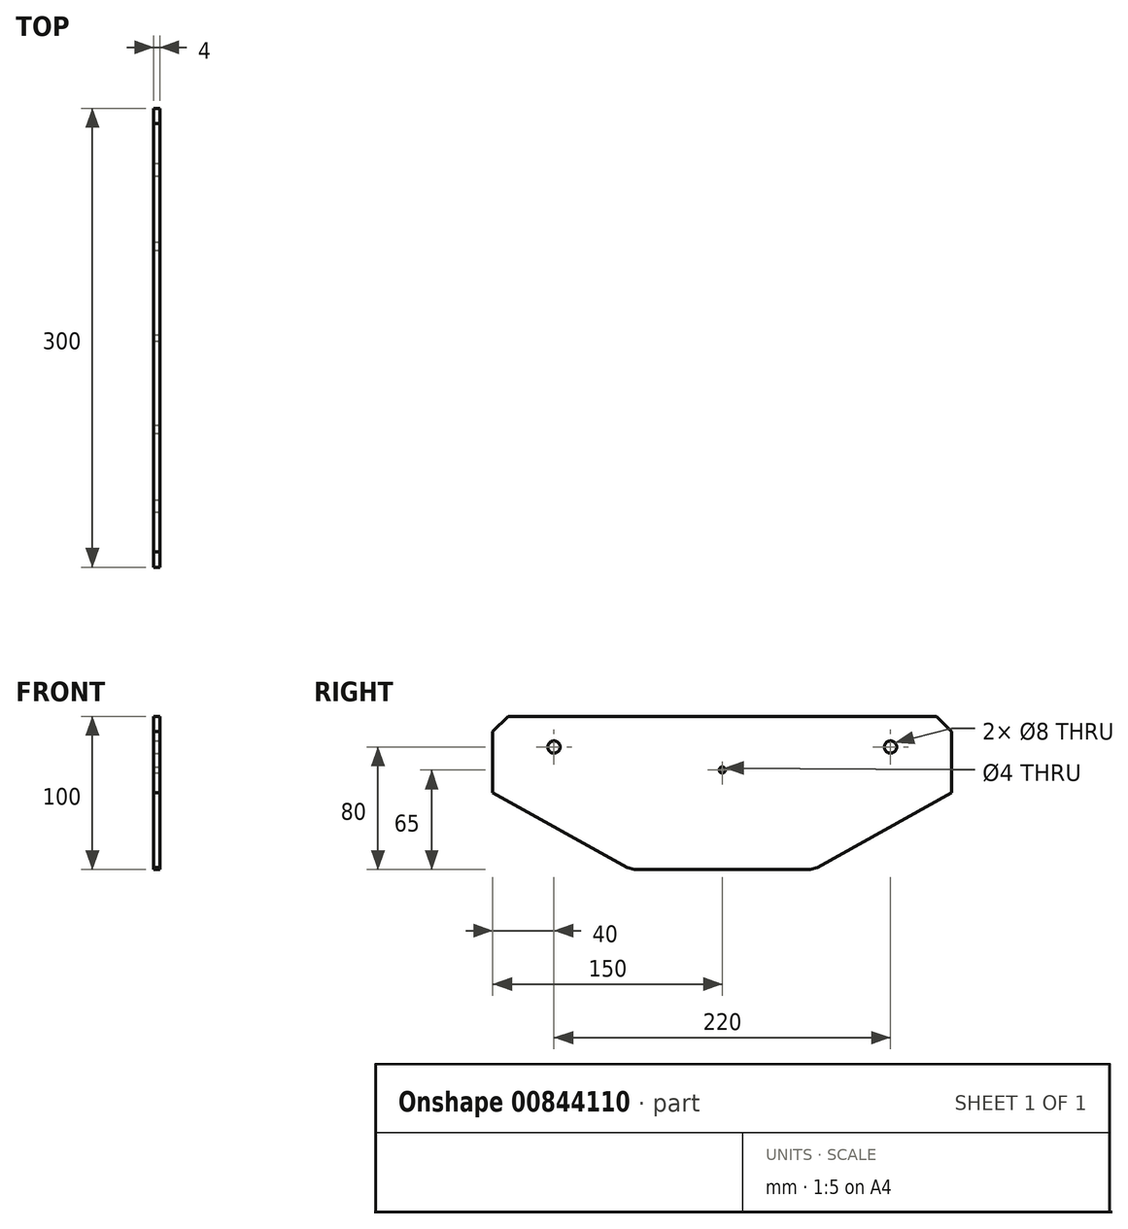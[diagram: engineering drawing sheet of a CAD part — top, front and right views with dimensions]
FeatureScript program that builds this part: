
annotation { "Feature Type Name" : "Feature", "Feature Type Description" : "" }
export const myFeature = defineFeature(function(context is Context, id is Id, definition is map)
    precondition{}
    {
        {
            var Q0;
            Q0=qCreatedBy(makeId("Right.planeOp"),FACE);
            var sketch = newSketch(context, id + "F0", { "sketchPlane" : qUnion([Q0])});
            skLineSegment(sketch, "E0", {"start": v(-150, 100) * mm, "end": v(150, 100) * mm});
            skLineSegment(sketch, "E1", {"start": v(150, 100) * mm, "end": v(150, 50) * mm});
            skLineSegment(sketch, "E2", {"start": v(150, 50) * mm, "end": v(60, 0) * mm});
            skLineSegment(sketch, "E3", {"start": v(60, 0) * mm, "end": v(-60, 0) * mm});
            skLineSegment(sketch, "E4", {"start": v(-60, 0) * mm, "end": v(-150, 50) * mm});
            skLineSegment(sketch, "E5", {"start": v(-150, 50) * mm, "end": v(-150, 100) * mm});
            skSolve(sketch);
        }
        {
            var Q0;
            Q0=makeQuery(id+"F0.imprint","IMPRINT",FACE,{"disambiguationData":[TD([[makeQuery(id+"F0.imprint","IMPRINT",EDGE,{"derivedFrom":sQuery(id+"F0.wireOp",EDGE,"E0")}),-1.0]])]});
            extrude(context, id + "F1", {"entities" : qUnion([Q0]), "endBound" : BoundingType.SYMMETRIC, "depth" : 4 * mm, "offsetDistance" : 25.4 * mm});
        }
        {
            var Q0;
            Q0=makeQuery(id+"F1.opExtrude","CAP_FACE",FACE,{"disambiguationData":[OSD([sQuery(id+"F0.wireOp",EDGE,"E0"),sQuery(id+"F0.wireOp",EDGE,"E1"),sQuery(id+"F0.wireOp",EDGE,"E2"),sQuery(id+"F0.wireOp",EDGE,"E3"),sQuery(id+"F0.wireOp",EDGE,"E4"),sQuery(id+"F0.wireOp",EDGE,"E5")])],"isStart":false});
            var sketch = newSketch(context, id + "F2", { "sketchPlane" : qUnion([Q0])});
            skPoint(sketch, "E6", {"position": v(-110, 80) * mm});
            skPoint(sketch, "E7", {"position": v(110, 80) * mm});
            skPoint(sketch, "E8", {"position": v(-60, -20) * mm});
            skPoint(sketch, "E9", {"position": v(60, -20) * mm});
            skPoint(sketch, "E10", {"position": v(0, -20) * mm});
            skPoint(sketch, "E11", {"position": v(0, 65) * mm});
            skSolve(sketch);
        }
        {
            var Q0;
            Q0=sQuery(id+"F2.wireOp",VERTEX,"E6");
            var Q1;
            Q1=sQuery(id+"F2.wireOp",VERTEX,"E7");
            var Q2;
            Q2=makeQuery(id+"F1.opExtrude","SWEPT_BODY",BODY,{"disambiguationData":[OSD([sQuery(id+"F0.wireOp",EDGE,"E0"),sQuery(id+"F0.wireOp",EDGE,"E1"),sQuery(id+"F0.wireOp",EDGE,"E2"),sQuery(id+"F0.wireOp",EDGE,"E3"),sQuery(id+"F0.wireOp",EDGE,"E4"),sQuery(id+"F0.wireOp",EDGE,"E5")])]});
            hole(context, id + "F3", {"style" : HoleStyle.SIMPLE, "endStyle" : HoleEndStyle.THROUGH, "holeDiameter" : 8 * mm, "majorDiameter" : 6.35 * mm, "isTappedThrough" : true, "tappedDepth" : 12.7 * mm, "tapClearance" : 3, "locations" : qUnion([Q0, Q1]), "scope" : qUnion([Q2])});
        }
        {
            var Q0;
            Q0=sQuery(id+"F2.wireOp",VERTEX,"E8");
            var Q1;
            Q1=sQuery(id+"F2.wireOp",VERTEX,"E10");
            var Q2;
            Q2=sQuery(id+"F2.wireOp",VERTEX,"E9");
            var Q3;
            Q3=makeQuery(id+"F1.opExtrude","SWEPT_BODY",BODY,{"disambiguationData":[OSD([sQuery(id+"F0.wireOp",EDGE,"E0"),sQuery(id+"F0.wireOp",EDGE,"E1"),sQuery(id+"F0.wireOp",EDGE,"E2"),sQuery(id+"F0.wireOp",EDGE,"E3"),sQuery(id+"F0.wireOp",EDGE,"E4"),sQuery(id+"F0.wireOp",EDGE,"E5")])]});
            hole(context, id + "F4", {"style" : HoleStyle.SIMPLE, "endStyle" : HoleEndStyle.THROUGH, "holeDiameter" : 4 * mm, "majorDiameter" : 6.35 * mm, "isTappedThrough" : true, "tappedDepth" : 12.7 * mm, "tapClearance" : 3, "locations" : qUnion([Q0, Q1, Q2]), "scope" : qUnion([Q3])});
        }
        {
            var Q0;
            Q0=makeQuery(id+"F1.opExtrude","SWEPT_EDGE",EDGE,{"disambiguationData":[OSD([sQuery(id+"F0.wireOp",EDGE,"E0"),sQuery(id+"F0.wireOp",EDGE,"E1")])]});
            var Q1;
            Q1=makeQuery(id+"F1.opExtrude","SWEPT_EDGE",EDGE,{"disambiguationData":[OSD([sQuery(id+"F0.wireOp",EDGE,"E0"),sQuery(id+"F0.wireOp",EDGE,"E5")])]});
            var Q2;
            Q2=makeQuery(id+"F1.opExtrude","SWEPT_EDGE",EDGE,{"disambiguationData":[OSD([sQuery(id+"F0.wireOp",EDGE,"E3"),sQuery(id+"F0.wireOp",EDGE,"E4")])]});
            var Q3;
            Q3=makeQuery(id+"F1.opExtrude","SWEPT_EDGE",EDGE,{"disambiguationData":[OSD([sQuery(id+"F0.wireOp",EDGE,"E2"),sQuery(id+"F0.wireOp",EDGE,"E3")])]});
            chamfer(context, id + "F5", {"entities" : qUnion([Q0, Q1, Q2, Q3]), "width" : 10 * mm, "tangentPropagation" : true});
        }
        {
            var Q0;
            Q0=sQuery(id+"F2.wireOp",VERTEX,"E11");
            var Q1;
            Q1=makeQuery(id+"F1.opExtrude","SWEPT_BODY",BODY,{"disambiguationData":[OSD([sQuery(id+"F0.wireOp",EDGE,"E0"),sQuery(id+"F0.wireOp",EDGE,"E1"),sQuery(id+"F0.wireOp",EDGE,"E2"),sQuery(id+"F0.wireOp",EDGE,"E3"),sQuery(id+"F0.wireOp",EDGE,"E4"),sQuery(id+"F0.wireOp",EDGE,"E5")])]});
            hole(context, id + "F6", {"style" : HoleStyle.SIMPLE, "endStyle" : HoleEndStyle.THROUGH, "holeDiameter" : 4 * mm, "majorDiameter" : 5 * mm, "isTappedThrough" : true, "tappedDepth" : 12.7 * mm, "tapClearance" : 3, "locations" : qUnion([Q0]), "scope" : qUnion([Q1])});
        }
    });
